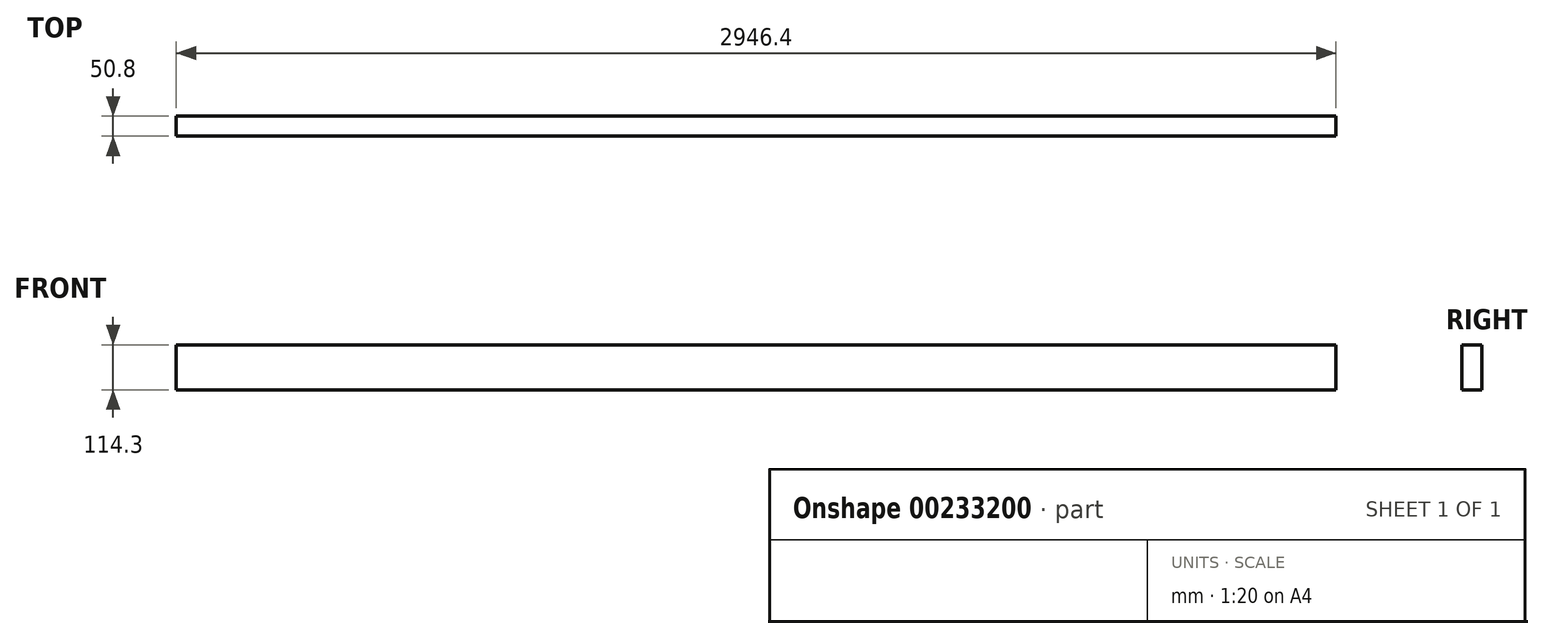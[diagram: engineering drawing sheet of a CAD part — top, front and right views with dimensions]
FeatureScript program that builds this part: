
annotation { "Feature Type Name" : "Feature", "Feature Type Description" : "" }
export const myFeature = defineFeature(function(context is Context, id is Id, definition is map)
    precondition{}
    {
        {
            var Q0;
            Q0=qCreatedBy(makeId("Top.planeOp"),FACE);
            var sketch = newSketch(context, id + "F0", { "sketchPlane" : qUnion([Q0])});
            skLineSegment(sketch, "E0.bottom", {"start": v(-1475.91, -453.96) * mm, "end": v(1470.49, -453.96) * mm});
            skLineSegment(sketch, "E0.top", {"start": v(-1475.91, -504.76) * mm, "end": v(1470.49, -504.76) * mm});
            skLineSegment(sketch, "E0.left", {"start": v(-1475.91, -453.96) * mm, "end": v(-1475.91, -504.76) * mm});
            skLineSegment(sketch, "E0.right", {"start": v(1470.49, -453.96) * mm, "end": v(1470.49, -504.76) * mm});
            skSolve(sketch);
        }
        {
            var Q0;
            Q0=makeQuery(id+"F0.imprint","IMPRINT",FACE,{"disambiguationData":[TD([[makeQuery(id+"F0.imprint","IMPRINT",EDGE,{"derivedFrom":sQuery(id+"F0.wireOp",EDGE,"E0.bottom")}),-1.0]])]});
            extrude(context, id + "F1", {"entities" : qUnion([Q0]), "depth" : 114.3 * mm});
        }
    });
